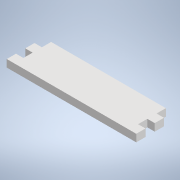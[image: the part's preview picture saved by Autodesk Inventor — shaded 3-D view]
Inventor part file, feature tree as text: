
AUTODESK INVENTOR PART (.ipt)
format: ipt  version: 2020.2 (Build 242310000, 310)  size: 112,640 bytes
history: native  units: mm
features: extrude x2, sketch x2
ambient origin geometry x8: Origin, YZ Plane, XZ Plane, XY Plane, X Axis, Y Axis, Z Axis, Center Point
bodies: Solido1 (feature_tree)
feature tree (4):
  extrude  "Estrusione1"  Depth=70.0mm
  extrude  "Estrusione2"  Depth=20.0mm
  sketch  "Schizzo1"
  sketch  "Schizzo2"
